# Revit family: HVAC_Air-Conditioning_Friedrich_Variable-Refrigerant-Packaged-Heat-Pump_VRP36K
name_source: partatom
category: Mechanical Equipment
revit_build: Autodesk Revit 2015 (Build: 20140606_1530(x64)
units: mm (PartAtom-declared; Revit-internal decimal feet)

## types (1)
- VRP36K
    Air Flow = 1200.0 CFM
    Air Supply Depth = 6.5 "
    Air Supply Width = 24 "
    BIMobject category = Air Conditioning
    BIMobject category code = hvac-air-con
    BIMobject main category = HVAC
    BIMobject main category code = hvac
    Brand url = http://friedrich.com
    COP = 3.25
    Cooling = 33400 Btu/h
    Cooling Current = 14 A
    Cooling Range = 20000-36000
    Depth = 29.88 "
    Description = Precision Inverter® compressor delivers best in class cooling performance with efficiencies up to 20 SEER. Super efficient heating with low-ambient heat pump operation to 0˚ F*.
    Design country = United States
    EER Rating = 11
    Edition number = 1
    Filter Material = Filter - Friedrich - Grey
    Heat Pump Current = 12 A
    Heating Power = 2570 W
    Heating Seasonal Performance Factor = 8.6
    Height = 77.25 "
    IFC Classification = Air Terminal
    Load Classification = HVAC
    Main Material = Metal - Friedrich - White
    Manufacturer = Friedrich
    Manufacturer country = Mexico
    Manufacturer name = Friedrich
    Masterformat 2014 Code = 23 81 13
    Masterformat 2014 Description = Packaged Terminal Air-Conditioners
    Material main = Metal
    Model = VRP36K
    NBS Reference Code = 68-38
    NBS Reference Description = Heat Pumps
    Nominal height = 0 "
    Nominal width = 0 "
    OmniClass Code = 23-33 17 00
    OmniClass Description = Heat Pumps
    Outdoor Operating Range = 55-115 (°F)
    Product Guid = 43060c2a-88f4-4ab8-9165-9feaed4c8084
    Product SKU = VRP36
    Product certification = https://cdn2.hubspot.net
    Product data url = https://bimobject.com
    Product family = Variable Refrigerant Package
    Product group = VRP
    Product url = https://www.friedrich.com
    QR code = http://bimobject.com
    Return Air Depth = 20 "
    Return Air Width = 30 "
    SEER = 15.5
    Technical description = https://cdn2.hubspot.net
    Total Heating Capacity = 28500 Btu/h
    UNSPSC Code = 40101806
    URL = https://www.friedrich.com
    Uniclass 1.4 Code = L7524
    Uniclass 1.4 Description = Heat pumps
    Uniclass 2.0 Code = PR-68-38
    Uniclass 2.0 Description = Heat Pumps
    Uniclass 2015 Code = Pr_70_60_37
    Uniclass 2015 Name = Heat pumps
    Uniformat II Code = D3050
    Uniformat II Description = Terminal & Package Units
    Voltage = 230 V
    Voltage Range = 208-230
    Weight = 330.00 lbm
    Weight Net (Kg) = 0
    Width = 31.75 "
    Youtube clip = https://youtu.be

## geometry (parser evidence)
native form markers: Sweep x3
no freeform markers — native parametric forms only
